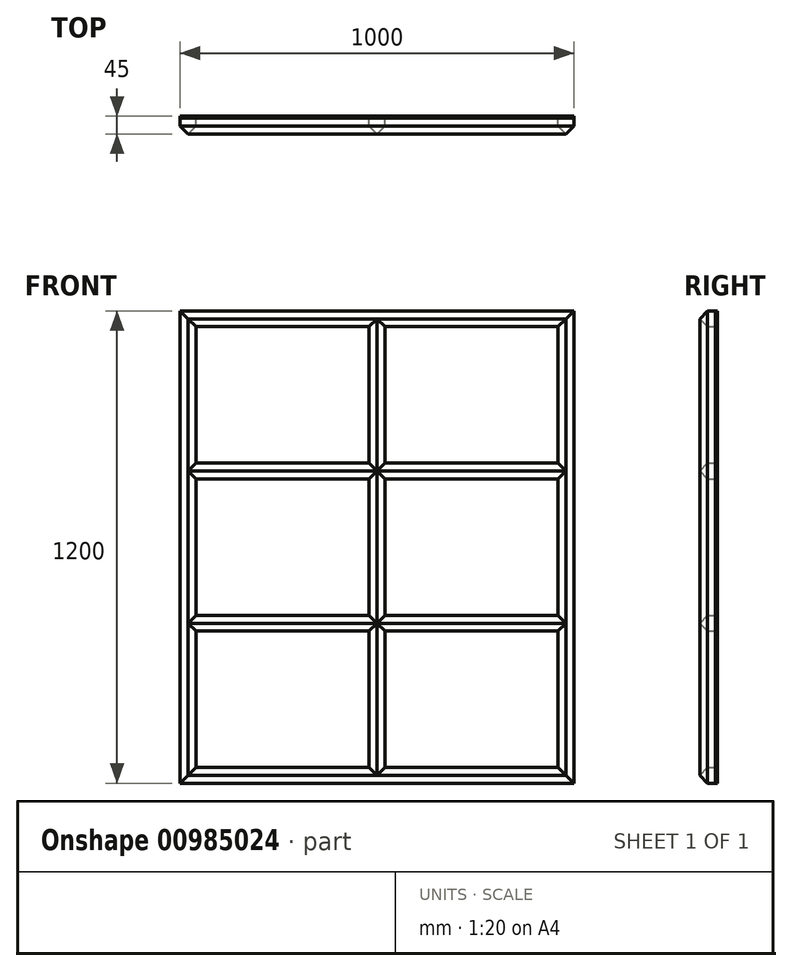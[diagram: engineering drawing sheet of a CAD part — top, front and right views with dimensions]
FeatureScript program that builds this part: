
annotation { "Feature Type Name" : "Feature", "Feature Type Description" : "" }
export const myFeature = defineFeature(function(context is Context, id is Id, definition is map)
    precondition{}
    {
        {
            var Q0;
            Q0=qCreatedBy(makeId("Front.planeOp"),FACE);
            var sketch = newSketch(context, id + "F0", { "sketchPlane" : qUnion([Q0])});
            skLineSegment(sketch, "E0.bottom", {"start": v(-520, 386.67) * mm, "end": v(480, 386.67) * mm});
            skLineSegment(sketch, "E0.top", {"start": v(-520, -813.33) * mm, "end": v(480, -813.33) * mm});
            skLineSegment(sketch, "E0.left", {"start": v(-520, 386.67) * mm, "end": v(-520, -813.33) * mm});
            skLineSegment(sketch, "E0.right", {"start": v(480, 386.67) * mm, "end": v(480, -813.33) * mm});
            skLineSegment(sketch, "E1.bottom", {"start": v(-480, 346.67) * mm, "end": v(-40, 346.67) * mm});
            skLineSegment(sketch, "E1.top", {"start": v(-480, 0) * mm, "end": v(-40, 0) * mm});
            skLineSegment(sketch, "E1.left", {"start": v(-480, 346.67) * mm, "end": v(-480, 0) * mm});
            skLineSegment(sketch, "E1.right", {"start": v(-40, 346.67) * mm, "end": v(-40, 0) * mm});
            skLineSegment(sketch, "E2.bottom", {"start": v(0, 346.67) * mm, "end": v(440, 346.67) * mm});
            skLineSegment(sketch, "E2.top", {"start": v(0, 0) * mm, "end": v(440, 0) * mm});
            skLineSegment(sketch, "E2.left", {"start": v(0, 346.67) * mm, "end": v(0, 0) * mm});
            skLineSegment(sketch, "E2.right", {"start": v(440, 346.67) * mm, "end": v(440, 0) * mm});
            skLineSegment(sketch, "E3.bottom", {"start": v(-480, -40) * mm, "end": v(-40, -40) * mm});
            skLineSegment(sketch, "E3.top", {"start": v(-480, -386.67) * mm, "end": v(-40, -386.67) * mm});
            skLineSegment(sketch, "E3.left", {"start": v(-480, -40) * mm, "end": v(-480, -386.67) * mm});
            skLineSegment(sketch, "E3.right", {"start": v(-40, -40) * mm, "end": v(-40, -386.67) * mm});
            skLineSegment(sketch, "E4.bottom", {"start": v(0, -40) * mm, "end": v(440, -40) * mm});
            skLineSegment(sketch, "E4.top", {"start": v(0, -386.67) * mm, "end": v(440, -386.67) * mm});
            skLineSegment(sketch, "E4.left", {"start": v(0, -40) * mm, "end": v(0, -386.67) * mm});
            skLineSegment(sketch, "E4.right", {"start": v(440, -40) * mm, "end": v(440, -386.67) * mm});
            skLineSegment(sketch, "E5.bottom", {"start": v(-480, -426.67) * mm, "end": v(-40, -426.67) * mm});
            skLineSegment(sketch, "E5.top", {"start": v(-480, -773.33) * mm, "end": v(-40, -773.33) * mm});
            skLineSegment(sketch, "E5.left", {"start": v(-480, -426.67) * mm, "end": v(-480, -773.33) * mm});
            skLineSegment(sketch, "E5.right", {"start": v(-40, -426.67) * mm, "end": v(-40, -773.33) * mm});
            skLineSegment(sketch, "E6.bottom", {"start": v(0, -426.67) * mm, "end": v(440, -426.67) * mm});
            skLineSegment(sketch, "E6.top", {"start": v(0, -773.33) * mm, "end": v(440, -773.33) * mm});
            skLineSegment(sketch, "E6.left", {"start": v(0, -426.67) * mm, "end": v(0, -773.33) * mm});
            skLineSegment(sketch, "E6.right", {"start": v(440, -426.67) * mm, "end": v(440, -773.33) * mm});
            skSolve(sketch);
        }
        {
            var Q0;
            Q0=makeQuery(id+"F0.imprint","IMPRINT",FACE,{"disambiguationData":[TD([[makeQuery(id+"F0.imprint","IMPRINT",EDGE,{"derivedFrom":sQuery(id+"F0.wireOp",EDGE,"E0.bottom")}),-1.0]])]});
            extrude(context, id + "F1", {"entities" : qUnion([Q0]), "depth" : 40 * mm, "offsetDistance" : 25 * mm});
        }
        {
            var Q0;
            Q0=makeQuery(id+"F1.opExtrude","CAP_FACE",FACE,{"disambiguationData":[OSD([sQuery(id+"F0.wireOp",EDGE,"E0.bottom"),sQuery(id+"F0.wireOp",EDGE,"E0.top"),sQuery(id+"F0.wireOp",EDGE,"E0.left"),sQuery(id+"F0.wireOp",EDGE,"E0.right"),sQuery(id+"F0.wireOp",EDGE,"E1.bottom"),sQuery(id+"F0.wireOp",EDGE,"E1.top"),sQuery(id+"F0.wireOp",EDGE,"E1.left"),sQuery(id+"F0.wireOp",EDGE,"E1.right"),sQuery(id+"F0.wireOp",EDGE,"E2.bottom"),sQuery(id+"F0.wireOp",EDGE,"E2.top"),sQuery(id+"F0.wireOp",EDGE,"E2.left"),sQuery(id+"F0.wireOp",EDGE,"E2.right"),sQuery(id+"F0.wireOp",EDGE,"E3.bottom"),sQuery(id+"F0.wireOp",EDGE,"E3.top"),sQuery(id+"F0.wireOp",EDGE,"E3.left"),sQuery(id+"F0.wireOp",EDGE,"E3.right"),sQuery(id+"F0.wireOp",EDGE,"E4.bottom"),sQuery(id+"F0.wireOp",EDGE,"E4.top"),sQuery(id+"F0.wireOp",EDGE,"E4.left"),sQuery(id+"F0.wireOp",EDGE,"E4.right"),sQuery(id+"F0.wireOp",EDGE,"E5.bottom"),sQuery(id+"F0.wireOp",EDGE,"E5.top"),sQuery(id+"F0.wireOp",EDGE,"E5.left"),sQuery(id+"F0.wireOp",EDGE,"E5.right"),sQuery(id+"F0.wireOp",EDGE,"E6.bottom"),sQuery(id+"F0.wireOp",EDGE,"E6.top"),sQuery(id+"F0.wireOp",EDGE,"E6.left"),sQuery(id+"F0.wireOp",EDGE,"E6.right")])],"isStart":false});
            chamfer(context, id + "F2", {"entities" : qUnion([Q0]), "width" : 20 * mm, "tangentPropagation" : true});
        }
        {
            var Q0;
            Q0=makeQuery(id+"F1.opExtrude","CAP_FACE",FACE,{"disambiguationData":[OSD([sQuery(id+"F0.wireOp",EDGE,"E0.bottom"),sQuery(id+"F0.wireOp",EDGE,"E0.top"),sQuery(id+"F0.wireOp",EDGE,"E0.left"),sQuery(id+"F0.wireOp",EDGE,"E0.right"),sQuery(id+"F0.wireOp",EDGE,"E1.bottom"),sQuery(id+"F0.wireOp",EDGE,"E1.top"),sQuery(id+"F0.wireOp",EDGE,"E1.left"),sQuery(id+"F0.wireOp",EDGE,"E1.right"),sQuery(id+"F0.wireOp",EDGE,"E2.bottom"),sQuery(id+"F0.wireOp",EDGE,"E2.top"),sQuery(id+"F0.wireOp",EDGE,"E2.left"),sQuery(id+"F0.wireOp",EDGE,"E2.right"),sQuery(id+"F0.wireOp",EDGE,"E3.bottom"),sQuery(id+"F0.wireOp",EDGE,"E3.top"),sQuery(id+"F0.wireOp",EDGE,"E3.left"),sQuery(id+"F0.wireOp",EDGE,"E3.right"),sQuery(id+"F0.wireOp",EDGE,"E4.bottom"),sQuery(id+"F0.wireOp",EDGE,"E4.top"),sQuery(id+"F0.wireOp",EDGE,"E4.left"),sQuery(id+"F0.wireOp",EDGE,"E4.right"),sQuery(id+"F0.wireOp",EDGE,"E5.bottom"),sQuery(id+"F0.wireOp",EDGE,"E5.top"),sQuery(id+"F0.wireOp",EDGE,"E5.left"),sQuery(id+"F0.wireOp",EDGE,"E5.right"),sQuery(id+"F0.wireOp",EDGE,"E6.bottom"),sQuery(id+"F0.wireOp",EDGE,"E6.top"),sQuery(id+"F0.wireOp",EDGE,"E6.left"),sQuery(id+"F0.wireOp",EDGE,"E6.right")])],"isStart":true});
            var sketch = newSketch(context, id + "F3", { "sketchPlane" : qUnion([Q0])});
            skLineSegment(sketch, "E7.bottom", {"start": v(-480, 386.67) * mm, "end": v(520, 386.67) * mm});
            skLineSegment(sketch, "E7.top", {"start": v(-480, -813.33) * mm, "end": v(520, -813.33) * mm});
            skLineSegment(sketch, "E7.left", {"start": v(-480, 386.67) * mm, "end": v(-480, -813.33) * mm});
            skLineSegment(sketch, "E7.right", {"start": v(520, 386.67) * mm, "end": v(520, -813.33) * mm});
            skSolve(sketch);
        }
        {
            var Q0;
            Q0 = qSketchRegion(id + "F3", true);
            extrude(context, id + "F4", {"entities" : qUnion([Q0]), "depth" : 5 * mm, "offsetDistance" : 25 * mm});
        }
    });
